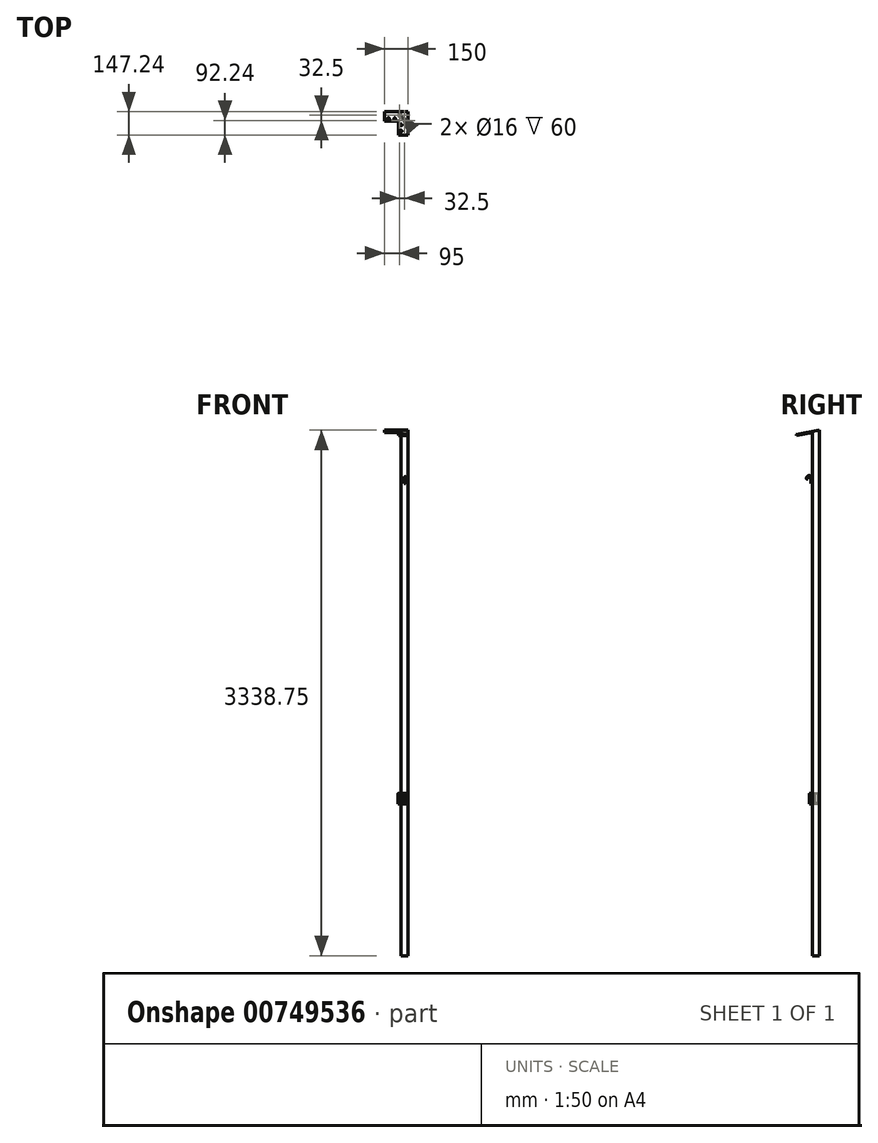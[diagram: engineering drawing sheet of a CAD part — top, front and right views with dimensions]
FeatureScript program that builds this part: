
annotation { "Feature Type Name" : "Feature", "Feature Type Description" : "" }
export const myFeature = defineFeature(function(context is Context, id is Id, definition is map)
    precondition{}
    {
        {
            var Q0;
            Q0=qCreatedBy(makeId("Top.planeOp"),FACE);
            var sketch = newSketch(context, id + "F0", { "sketchPlane" : qUnion([Q0])});
            skLineSegment(sketch, "E0.bottom", {"start": v(22.5, -22.5) * mm, "end": v(-22.5, -22.5) * mm});
            skLineSegment(sketch, "E0.top", {"start": v(22.5, 22.5) * mm, "end": v(-22.5, 22.5) * mm});
            skLineSegment(sketch, "E0.left", {"start": v(22.5, -22.5) * mm, "end": v(22.5, 22.5) * mm});
            skLineSegment(sketch, "E0.right", {"start": v(-22.5, -22.5) * mm, "end": v(-22.5, 22.5) * mm});
            skPoint(sketch, "E0.middle", {"position": v(0, 0) * mm});
            skSolve(sketch);
        }
        {
            var Q0;
            Q0=qSketchRegion(id+"F0",true);
            extrude(context, id + "F1", {"entities" : qUnion([Q0]), "depth" : 3330 * mm, "offsetDistance" : 25 * mm});
        }
        {
            var Q0;
            Q0=qCreatedBy(makeId("Top.planeOp"),FACE);
            cPlane(context, id + "F2", {"entities" : qUnion([Q0]), "cplaneType" : CPlaneType.OFFSET, "offset" : 965 * mm, "width" : 150 * mm, "height" : 150 * mm});
        }
        {
            var Q0;
            Q0=qCreatedBy(id+"F2.planeOp",FACE);
            var sketch = newSketch(context, id + "F3", { "sketchPlane" : qUnion([Q0])});
            skLineSegment(sketch, "E1", {"start": v(0, -22.5) * mm, "end": v(0, -32.5) * mm});
            skArc(sketch, "E2", {"start": v(-2, -22.7) * mm, "mid": v(0, -42.5) * mm, "end": v(2, -22.7) * mm});
            skLineSegment(sketch, "E3", {"start": v(0, 0) * mm, "end": v(22.5, 0) * mm});
            skLineSegment(sketch, "E4", {"start": v(0, -32.5) * mm, "end": v(2, -32.5) * mm});
            skLineSegment(sketch, "E5", {"start": v(0, -32.5) * mm, "end": v(-2, -32.5) * mm});
            skLineSegment(sketch, "E6", {"start": v(2, -32.5) * mm, "end": v(2, -22.5) * mm});
            skLineSegment(sketch, "E7", {"start": v(-2, -32.5) * mm, "end": v(-2, -22.5) * mm});
            skLineSegment(sketch, "E8", {"start": v(0, 0) * mm, "end": v(-22.5, 0) * mm});
            skLineSegment(sketch, "E9", {"start": v(-22.5, 0) * mm, "end": v(-32.5, 0) * mm});
            skCircle(sketch, "E10", {"center": v(-32.5, 0) * mm, "radius": 10 * mm});
            skLineSegment(sketch, "E11", {"start": v(-2, -32.5) * mm, "end": v(-10, -32.5) * mm});
            skLineSegment(sketch, "E12", {"start": v(-10, -32.5) * mm, "end": v(-10, -22.5) * mm});
            skLineSegment(sketch, "E13", {"start": v(2, -32.5) * mm, "end": v(10, -32.5) * mm});
            skLineSegment(sketch, "E14", {"start": v(10, -32.5) * mm, "end": v(10, -22.5) * mm});
            skLineSegment(sketch, "E15", {"start": v(-10, -22.5) * mm, "end": v(10, -22.5) * mm});
            skLineSegment(sketch, "E16", {"start": v(-32.5, 0) * mm, "end": v(-32.5, -10) * mm});
            skLineSegment(sketch, "E17", {"start": v(-32.5, -10) * mm, "end": v(-22.5, -10) * mm});
            skLineSegment(sketch, "E18", {"start": v(-32.5, 0) * mm, "end": v(-32.5, 10) * mm});
            skLineSegment(sketch, "E19", {"start": v(-32.5, 10) * mm, "end": v(-22.5, 10) * mm});
            skLineSegment(sketch, "E20", {"start": v(-22.5, -10) * mm, "end": v(-22.5, 10) * mm});
            skSolve(sketch);
        }
        {
            var Q0;
            {var subQ0=sQuery(id+"F3.wireOp",EDGE,"E1");Q0=makeQuery(id+"F3.imprint","IMPRINT",FACE,{"disambiguationData":[TD([[makeQuery(id+"F3.imprint","IMPRINT",EDGE,{"derivedFrom":subQ0}),1.0]])]});}
            var Q1;
            {var subQ0=sQuery(id+"F3.wireOp",EDGE,"E1");Q1=makeQuery(id+"F3.imprint","IMPRINT",FACE,{"disambiguationData":[TD([[makeQuery(id+"F3.imprint","IMPRINT",EDGE,{"derivedFrom":subQ0}),-1.0]])]});}
            var Q2;
            {var subQ1=sQuery(id+"F3.wireOp",EDGE,"E4");Q2=makeQuery(id+"F3.imprint","IMPRINT",FACE,{"disambiguationData":[TD([[makeQuery(id+"F3.imprint","IMPRINT",EDGE,{"derivedFrom":subQ1}),-1.0]])]});}
            var Q3;
            Q3=makeQuery(id+"F3.imprint","IMPRINT",FACE,{"disambiguationData":[TD([[makeQuery(id+"F3.imprint","IMPRINT",EDGE,{"derivedFrom":sQuery(id+"F3.wireOp",EDGE,"E10")}),1.0]])]});
            var Q4;
            {var subQ3=sQuery(id+"F3.wireOp",EDGE,"E13");Q4=makeQuery(id+"F3.imprint","IMPRINT",FACE,{"disambiguationData":[TD([[makeQuery(id+"F3.imprint","IMPRINT",EDGE,{"derivedFrom":subQ3}),1.0]])]});}
            var Q5;
            {var subQ3=sQuery(id+"F3.wireOp",EDGE,"E14");Q5=makeQuery(id+"F3.imprint","IMPRINT",FACE,{"disambiguationData":[TD([[makeQuery(id+"F3.imprint","IMPRINT",EDGE,{"derivedFrom":subQ3}),1.0]])]});}
            var Q6;
            {var subQ3=sQuery(id+"F3.wireOp",EDGE,"E11");Q6=makeQuery(id+"F3.imprint","IMPRINT",FACE,{"disambiguationData":[TD([[makeQuery(id+"F3.imprint","IMPRINT",EDGE,{"derivedFrom":subQ3}),-1.0]])]});}
            var Q7;
            {var subQ3=sQuery(id+"F3.wireOp",EDGE,"E12");Q7=makeQuery(id+"F3.imprint","IMPRINT",FACE,{"disambiguationData":[TD([[makeQuery(id+"F3.imprint","IMPRINT",EDGE,{"derivedFrom":subQ3}),-1.0]])]});}
            var Q8;
            {var subQ3=sQuery(id+"F3.wireOp",EDGE,"E17");Q8=makeQuery(id+"F3.imprint","IMPRINT",FACE,{"disambiguationData":[TD([[makeQuery(id+"F3.imprint","IMPRINT",EDGE,{"derivedFrom":subQ3}),1.0]])]});}
            var Q9;
            {var subQ3=sQuery(id+"F3.wireOp",EDGE,"E19");Q9=makeQuery(id+"F3.imprint","IMPRINT",FACE,{"disambiguationData":[TD([[makeQuery(id+"F3.imprint","IMPRINT",EDGE,{"derivedFrom":subQ3}),-1.0]])]});}
            extrude(context, id + "F4", {"entities" : qUnion([Q0, Q1, Q2, Q3, Q4, Q5, Q6, Q7, Q8, Q9]), "operationType" : NewBodyOperationType.ADD, "depth" : 5 * mm, "offsetDistance" : 25 * mm});
        }
        {
            var Q0;
            Q0=makeQuery(id+"F1.opExtrude","CAP_EDGE",EDGE,{"disambiguationData":[OSD([sQuery(id+"F0.wireOp",EDGE,"E0.bottom")])],"isStart":false});
            cPlane(context, id + "F5", {"entities" : qUnion([Q0]), "cplaneType" : CPlaneType.LINE_ANGLE, "offset" : 25 * mm, "angle" : 101 * degree, "oppositeDirection" : true, "width" : 150 * mm, "height" : 150 * mm});
        }
        {
            var Q0;
            Q0=makeQuery(id+"F1.opExtrude","CAP_FACE",FACE,{"disambiguationData":[OSD([sQuery(id+"F0.wireOp",EDGE,"E0.bottom"),sQuery(id+"F0.wireOp",EDGE,"E0.top"),sQuery(id+"F0.wireOp",EDGE,"E0.left"),sQuery(id+"F0.wireOp",EDGE,"E0.right")])],"isStart":false});
            var sketch = newSketch(context, id + "F6", { "sketchPlane" : qUnion([Q0])});
            skLineSegment(sketch, "E21.bottom", {"start": v(-22.5, 22.5) * mm, "end": v(22.5, 22.5) * mm});
            skLineSegment(sketch, "E21.top", {"start": v(-22.5, -22.5) * mm, "end": v(22.5, -22.5) * mm});
            skLineSegment(sketch, "E21.left", {"start": v(-22.5, 22.5) * mm, "end": v(-22.5, -22.5) * mm});
            skLineSegment(sketch, "E21.right", {"start": v(22.5, 22.5) * mm, "end": v(22.5, -22.5) * mm});
            skSolve(sketch);
        }
        {
            var Q0;
            Q0=qCreatedBy(id+"F5.planeOp",FACE);
            var sketch = newSketch(context, id + "F7", { "sketchPlane" : qUnion([Q0])});
            skLineSegment(sketch, "E22.bottom", {"start": v(-22.5, -659.15) * mm, "end": v(22.5, -659.15) * mm});
            skLineSegment(sketch, "E22.top", {"start": v(-22.5, -613.3) * mm, "end": v(22.5, -613.3) * mm});
            skLineSegment(sketch, "E22.left", {"start": v(-22.5, -659.15) * mm, "end": v(-22.5, -613.3) * mm});
            skLineSegment(sketch, "E22.right", {"start": v(22.5, -659.15) * mm, "end": v(22.5, -613.3) * mm});
            skSolve(sketch);
        }
        {
            var Q0;
            Q0=makeQuery(id+"F7.imprint","IMPRINT",FACE,{"disambiguationData":[TD([[makeQuery(id+"F7.imprint","IMPRINT",EDGE,{"derivedFrom":sQuery(id+"F7.wireOp",EDGE,"E22.bottom")}),1.0]])]});
            extrude(context, id + "F8", {"entities" : qUnion([Q0]), "operationType" : NewBodyOperationType.ADD, "depth" : 25 * mm, "offsetDistance" : 25 * mm});
        }
        {
            var Q0;
            Q0=qCreatedBy(id+"F5.planeOp",FACE);
            var sketch = newSketch(context, id + "F9", { "sketchPlane" : qUnion([Q0])});
            skLineSegment(sketch, "E23.bottom", {"start": v(22.5, -659.15) * mm, "end": v(-127.5, -659.15) * mm});
            skLineSegment(sketch, "E23.top", {"start": v(22.5, -599.15) * mm, "end": v(-127.5, -599.15) * mm});
            skLineSegment(sketch, "E23.left", {"start": v(22.5, -659.15) * mm, "end": v(22.5, -599.15) * mm});
            skLineSegment(sketch, "E23.right", {"start": v(-127.5, -659.15) * mm, "end": v(-127.5, -599.15) * mm});
            skLineSegment(sketch, "E24", {"start": v(22.5, -659.15) * mm, "end": v(-37.5, -659.15) * mm});
            skLineSegment(sketch, "E25.bottom", {"start": v(-37.5, -659.15) * mm, "end": v(22.5, -659.15) * mm});
            skLineSegment(sketch, "E25.top", {"start": v(-37.5, -509.15) * mm, "end": v(22.5, -509.15) * mm});
            skLineSegment(sketch, "E25.left", {"start": v(-37.5, -659.15) * mm, "end": v(-37.5, -509.15) * mm});
            skLineSegment(sketch, "E25.right", {"start": v(22.5, -659.15) * mm, "end": v(22.5, -509.15) * mm});
            skSolve(sketch);
        }
        {
            var Q0;
            Q0=qSketchRegion(id+"F9",true);
            extrude(context, id + "F10", {"entities" : qUnion([Q0]), "operationType" : NewBodyOperationType.ADD, "depth" : 5 * mm, "offsetDistance" : 25 * mm});
        }
        {
            var Q0;
            Q0=makeQuery(id+"F10.boolean.opBoolean","MERGE",FACE,{"derivedFrom":[makeQuery(id+"F8.opExtrude","CAP_FACE",FACE,{"disambiguationData":[OSD([sQuery(id+"F7.wireOp",EDGE,"E22.bottom"),sQuery(id+"F7.wireOp",EDGE,"E22.top"),sQuery(id+"F7.wireOp",EDGE,"E22.left"),sQuery(id+"F7.wireOp",EDGE,"E22.right")])],"isStart":true}),makeQuery(id+"F10.opExtrude","CAP_FACE",FACE,{"disambiguationData":[OSD([sQuery(id+"F9.wireOp",EDGE,"8cb1c19a-3ec8-4bcf-bfa4-e708c15dc5ac.bottom"),sQuery(id+"F9.wireOp",EDGE,"74325b9e-44c1-4043-a874-969d41da8b4c.bottom"),sQuery(id+"F9.wireOp",EDGE,"74325b9e-44c1-4043-a874-969d41da8b4c.top"),sQuery(id+"F9.wireOp",EDGE,"74325b9e-44c1-4043-a874-969d41da8b4c.right"),sQuery(id+"F9.wireOp",EDGE,"880eba7a-782f-4c27-b6fe-715e12f068d6.top"),sQuery(id+"F9.wireOp",EDGE,"880eba7a-782f-4c27-b6fe-715e12f068d6.right"),sQuery(id+"F9.wireOp",EDGE,"59256244-9167-4ee1-a51c-4aa0c58c6036")])],"isStart":true})]});
            var sketch = newSketch(context, id + "F11", { "sketchPlane" : qUnion([Q0])});
            skLineSegment(sketch, "E26", {"start": v(-22.5, 471.42) * mm, "end": v(22.5, 471.42) * mm});
            skLineSegment(sketch, "E27", {"start": v(0, 471.42) * mm, "end": v(0, 519.36) * mm});
            skCircle(sketch, "E28.MirrorC", {"center": v(-22.5, 534.15) * mm, "radius": 6 * mm});
            skCircle(sketch, "E29.MirrorC", {"center": v(-22.5, 574.15) * mm, "radius": 6 * mm});
            skCircle(sketch, "E30.MirrorC", {"center": v(-62.5, 614.15) * mm, "radius": 6 * mm});
            skCircle(sketch, "E31.MirrorC", {"center": v(-102.5, 614.15) * mm, "radius": 6 * mm});
            skSolve(sketch);
        }
        {
            var Q0;
            Q0=qSketchRegion(id+"F11",true);
            extrude(context, id + "F12", {"entities" : qUnion([Q0]), "operationType" : NewBodyOperationType.REMOVE, "oppositeDirection" : true, "depth" : 25 * mm, "offsetDistance" : 25 * mm});
        }
        {
            var Q0;
            Q0=qCreatedBy(makeId("Top.planeOp"),FACE);
            var sketch = newSketch(context, id + "F13", { "sketchPlane" : qUnion([Q0])});
            skLineSegment(sketch, "E32.bottom", {"start": v(-22.5, 22.5) * mm, "end": v(127.5, 22.5) * mm});
            skLineSegment(sketch, "E32.top", {"start": v(-22.5, 27.27) * mm, "end": v(127.5, 27.27) * mm});
            skLineSegment(sketch, "E32.left", {"start": v(-22.5, 22.5) * mm, "end": v(-22.5, 27.27) * mm});
            skLineSegment(sketch, "E32.right", {"start": v(127.5, 22.5) * mm, "end": v(127.5, 27.27) * mm});
            skSolve(sketch);
        }
        {
            var Q0;
            Q0=qSketchRegion(id+"F13",true);
            extrude(context, id + "F14", {"entities" : qUnion([Q0]), "operationType" : NewBodyOperationType.REMOVE, "depth" : 3358.7 * mm, "offsetDistance" : 25 * mm});
        }
        {
            var Q0;
            Q0=makeQuery(id+"F4.opExtrude","CAP_FACE",FACE,{"disambiguationData":[OSD([sQuery(id+"F3.wireOp",EDGE,"E10")])],"isStart":false});
            var sketch = newSketch(context, id + "F15", { "sketchPlane" : qUnion([Q0])});
            skCircle(sketch, "E33", {"center": v(-32.5, 0) * mm, "radius": 8 * mm});
            skCircle(sketch, "E34", {"center": v(-32.5, 0) * mm, "radius": 10 * mm});
            skCircle(sketch, "E35", {"center": v(0, -32.5) * mm, "radius": 8 * mm});
            skLineSegment(sketch, "E36", {"start": v(0, -22.5) * mm, "end": v(0, 0) * mm});
            skLineSegment(sketch, "E37", {"start": v(0, -22.5) * mm, "end": v(0, -32.5) * mm});
            skCircle(sketch, "E38", {"center": v(0, -32.5) * mm, "radius": 10 * mm});
            skLineSegment(sketch, "E39.0", {"start": v(-32.5, -10) * mm, "end": v(-22.5, -10) * mm});
            skLineSegment(sketch, "E40.0", {"start": v(-22.5, -10) * mm, "end": v(-22.5, 10) * mm});
            skLineSegment(sketch, "E41.0", {"start": v(-32.5, 10) * mm, "end": v(-22.5, 10) * mm});
            skLineSegment(sketch, "E42.0", {"start": v(-10, -22.5) * mm, "end": v(10, -22.5) * mm});
            skLineSegment(sketch, "E43.0", {"start": v(-10, -32.5) * mm, "end": v(-10, -22.5) * mm});
            skLineSegment(sketch, "E44.0", {"start": v(10, -32.5) * mm, "end": v(10, -22.5) * mm});
            skLineSegment(sketch, "E45", {"start": v(0, -32.5) * mm, "end": v(-8, -32.5) * mm});
            skSolve(sketch);
        }
        {
            var Q0;
            Q0 = qSketchRegion(id + "F15", true);
            extrude(context, id + "F16", {"entities" : qUnion([Q0]), "operationType" : NewBodyOperationType.ADD, "depth" : 60 * mm, "offsetDistance" : 25 * mm});
        }
        {
            var Q0;
            Q0=qCreatedBy(makeId("Top.planeOp"),FACE);
            cPlane(context, id + "F17", {"entities" : qUnion([Q0]), "cplaneType" : CPlaneType.OFFSET, "offset" : 3000 * mm, "width" : 150 * mm, "height" : 150 * mm});
        }
        {
            var Q0;
            Q0=qCreatedBy(id+"F17.planeOp",FACE);
            var sketch = newSketch(context, id + "F18", { "sketchPlane" : qUnion([Q0])});
            skLineSegment(sketch, "E46", {"start": v(0, -22.5) * mm, "end": v(0, -27.5) * mm});
            skCircle(sketch, "E47", {"center": v(0, -27.5) * mm, "radius": 5 * mm});
            skLineSegment(sketch, "E48", {"start": v(0, -27.5) * mm, "end": v(5, -27.5) * mm});
            skLineSegment(sketch, "E49", {"start": v(5, -27.5) * mm, "end": v(5, -22.5) * mm});
            skLineSegment(sketch, "E50", {"start": v(5, -22.5) * mm, "end": v(-5, -22.5) * mm});
            skLineSegment(sketch, "E51", {"start": v(-5, -22.5) * mm, "end": v(-5, -27.5) * mm});
            skSolve(sketch);
        }
        {
            var Q0;
            Q0=makeQuery(id+"F14.boolean.opBoolean","COPY",FACE,{"derivedFrom":makeQuery(id+"F14.opExtrude","SWEPT_FACE",FACE,{"disambiguationData":[OSD([sQuery(id+"F13.wireOp",EDGE,"E32.left")])]})});
            var sketch = newSketch(context, id + "F19", { "sketchPlane" : qUnion([Q0])});
            skLineSegment(sketch, "E52", {"start": v(23.45, 3333.84) * mm, "end": v(22.5, 3333.65) * mm});
            skLineSegment(sketch, "E53", {"start": v(22.5, 3333.65) * mm, "end": v(22.5, 3338.75) * mm});
            skLineSegment(sketch, "E54", {"start": v(22.5, 3338.75) * mm, "end": v(23.45, 3333.84) * mm});
            skSolve(sketch);
        }
        {
            var Q0;
            Q0 = qSketchRegion(id + "F19", true);
            extrude(context, id + "F20", {"entities" : qUnion([Q0]), "operationType" : NewBodyOperationType.REMOVE, "oppositeDirection" : true, "depth" : 109 * mm, "offsetDistance" : 25 * mm});
        }
        {
            var Q0;
            Q0 = qSketchRegion(id + "F18", true);
            extrude(context, id + "F21", {"entities" : qUnion([Q0]), "operationType" : NewBodyOperationType.ADD, "depth" : 30 * mm, "offsetDistance" : 25 * mm});
        }
        {
            var Q0;
            Q0=makeQuery(id+"F21.opExtrude","CAP_FACE",FACE,{"disambiguationData":[OSD([sQuery(id+"F18.wireOp",EDGE,"E47"),sQuery(id+"F18.wireOp",EDGE,"E49"),sQuery(id+"F18.wireOp",EDGE,"E50"),sQuery(id+"F18.wireOp",EDGE,"E51")])],"isStart":false});
            var sketch = newSketch(context, id + "F22", { "sketchPlane" : qUnion([Q0])});
            skArc(sketch, "E55.0", {"start": v(-5, -27.5) * mm, "mid": v(0, -32.5) * mm, "end": v(5, -27.5) * mm});
            skLineSegment(sketch, "E56", {"start": v(0, -27.5) * mm, "end": v(5, -27.5) * mm});
            skArc(sketch, "E57.MirrorCS", {"start": v(-5, -27.5) * mm, "mid": v(0, -22.5) * mm, "end": v(5, -27.5) * mm});
            skSolve(sketch);
        }
        {
            var Q0;
            Q0=qCreatedBy(makeId("Right.planeOp"),FACE);
            var sketch = newSketch(context, id + "F23", { "sketchPlane" : qUnion([Q0])});
            skLineSegment(sketch, "E58", {"start": v(-27.5, 3030) * mm, "end": v(-57.5, 3030) * mm});
            skArc(sketch, "E59", {"start": v(-27.5, 3030) * mm, "mid": v(-42.5, 3045) * mm, "end": v(-57.5, 3030) * mm});
            skSolve(sketch);
        }
        {
            var Q0;
            {var subQ0=sQuery(id+"F22.wireOp",EDGE,"E55.0");Q0=makeQuery(id+"F22.imprint","IMPRINT",FACE,{"disambiguationData":[TD([[makeQuery(id+"F22.imprint","IMPRINT",EDGE,{"derivedFrom":subQ0}),1.0]])]});}
            var Q1;
            Q1=sQuery(id+"F23.wireOp",EDGE,"E59");
            sweep(context, id + "F24", {"operationType" : NewBodyOperationType.ADD, "profiles" : qUnion([Q0]), "path" : qUnion([Q1])});
        }
    });
